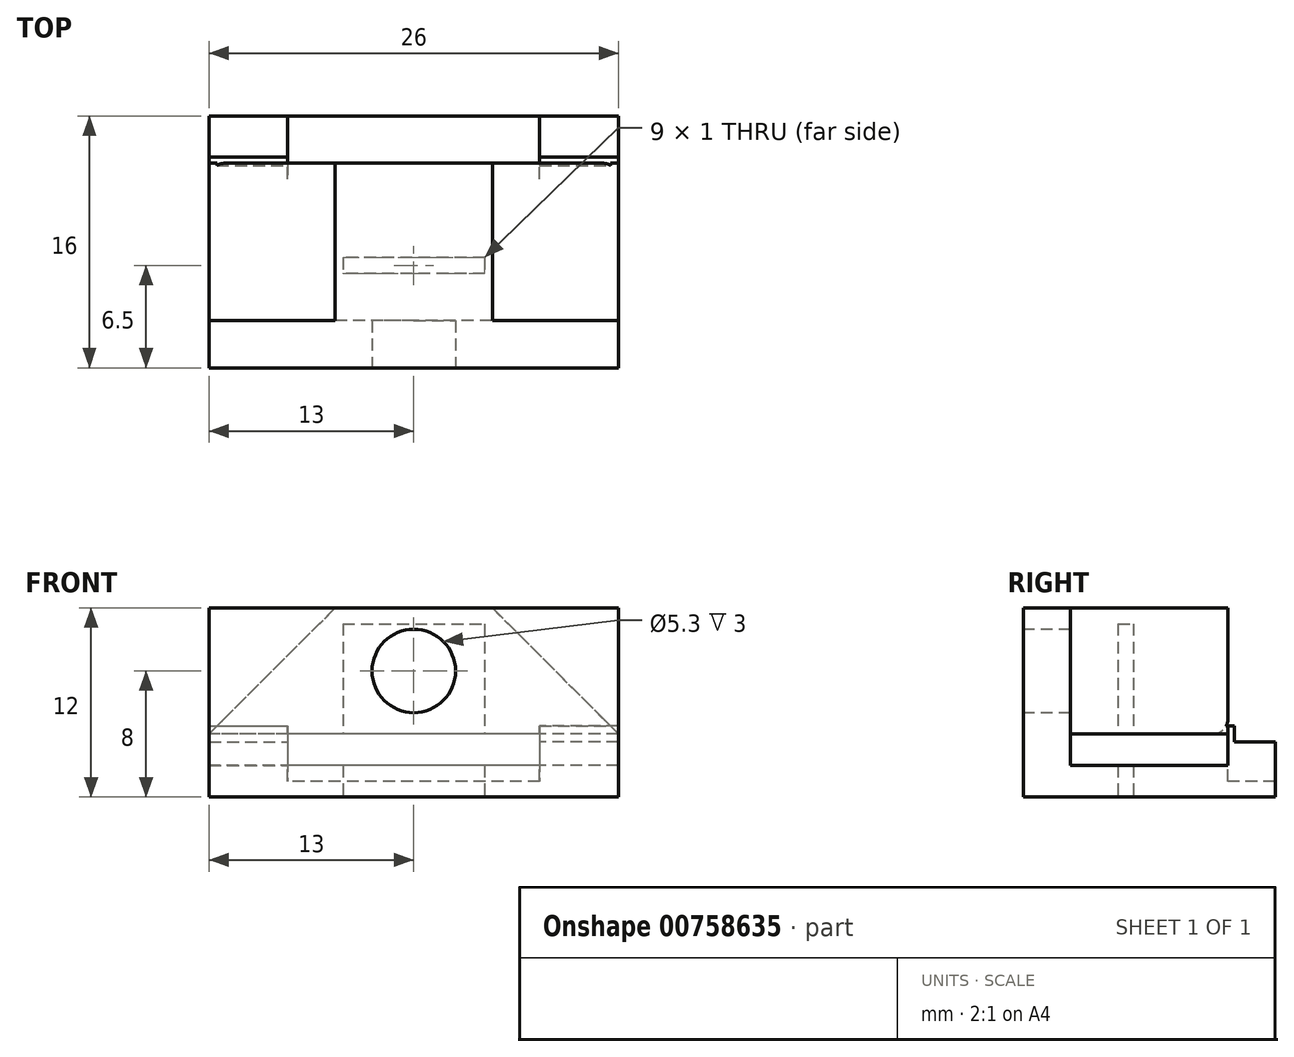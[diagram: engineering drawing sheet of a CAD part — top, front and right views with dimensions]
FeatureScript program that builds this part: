
annotation { "Feature Type Name" : "Feature", "Feature Type Description" : "" }
export const myFeature = defineFeature(function(context is Context, id is Id, definition is map)
    precondition{}
    {
        {
            var Q0;
            Q0=qCreatedBy(makeId("Front.planeOp"),FACE);
            var sketch = newSketch(context, id + "F0", { "sketchPlane" : qUnion([Q0])});
            skLineSegment(sketch, "E0.bottom", {"start": v(13, -6) * mm, "end": v(-13, -6) * mm});
            skLineSegment(sketch, "E0.top", {"start": v(13, 6) * mm, "end": v(-13, 6) * mm});
            skLineSegment(sketch, "E0.left", {"start": v(13, -6) * mm, "end": v(13, 6) * mm});
            skLineSegment(sketch, "E0.right", {"start": v(-13, -6) * mm, "end": v(-13, 6) * mm});
            skPoint(sketch, "E0.middle", {"position": v(0, 0) * mm});
            skSolve(sketch);
        }
        {
            var Q0;
            Q0 = qSketchRegion(id + "F0", true);
            extrude(context, id + "F1", {"entities" : qUnion([Q0]), "depth" : 3 * mm, "offsetDistance" : 25 * mm});
        }
        {
            var Q0;
            Q0=makeQuery(id+"F1.opExtrude","CAP_FACE",FACE,{"disambiguationData":[OSD([sQuery(id+"F0.wireOp",EDGE,"E0.bottom"),sQuery(id+"F0.wireOp",EDGE,"E0.top"),sQuery(id+"F0.wireOp",EDGE,"E0.left"),sQuery(id+"F0.wireOp",EDGE,"E0.right")])],"isStart":true});
            var sketch = newSketch(context, id + "F2", { "sketchPlane" : qUnion([Q0])});
            skLineSegment(sketch, "E1", {"start": v(0, -2) * mm, "end": v(13, -2) * mm});
            skPoint(sketch, "E1.startSnap0", {"position": v(0, 6) * mm});
            skLineSegment(sketch, "E2", {"start": v(13, -2) * mm, "end": v(5, 6) * mm});
            skLineSegment(sketch, "E3", {"start": v(5, 6) * mm, "end": v(0, 6) * mm});
            skLineSegment(sketch, "E4.MirrorCS", {"start": v(-5, 6) * mm, "end": v(0, 6) * mm});
            skLineSegment(sketch, "E5.MirrorCS", {"start": v(-13, -2) * mm, "end": v(-5, 6) * mm});
            skLineSegment(sketch, "E6.MirrorCS", {"start": v(0, -2) * mm, "end": v(-13, -2) * mm});
            skSolve(sketch);
        }
        {
            var Q0;
            Q0 = qSketchRegion(id + "F2", true);
            extrude(context, id + "F3", {"entities" : qUnion([Q0]), "depth" : 10 * mm, "offsetDistance" : 25 * mm});
        }
        {
            var Q0;
            Q0=makeQuery(id+"F1.opExtrude","CAP_FACE",FACE,{"disambiguationData":[OSD([sQuery(id+"F0.wireOp",EDGE,"E0.bottom"),sQuery(id+"F0.wireOp",EDGE,"E0.top"),sQuery(id+"F0.wireOp",EDGE,"E0.left"),sQuery(id+"F0.wireOp",EDGE,"E0.right")])],"isStart":true});
            var sketch = newSketch(context, id + "F4", { "sketchPlane" : qUnion([Q0])});
            skLineSegment(sketch, "E7.bottom", {"start": v(-13, -6) * mm, "end": v(13, -6) * mm});
            skLineSegment(sketch, "E7.top", {"start": v(-13, -4) * mm, "end": v(13, -4) * mm});
            skLineSegment(sketch, "E7.left", {"start": v(-13, -6) * mm, "end": v(-13, -4) * mm});
            skLineSegment(sketch, "E7.right", {"start": v(13, -6) * mm, "end": v(13, -4) * mm});
            skSolve(sketch);
        }
        {
            var Q0;
            Q0 = qSketchRegion(id + "F4", true);
            extrude(context, id + "F5", {"entities" : qUnion([Q0]), "operationType" : NewBodyOperationType.ADD, "depth" : 13 * mm, "offsetDistance" : 25 * mm});
        }
        {
            var Q0;
            Q0=makeQuery(id+"F5.opExtrude","SWEPT_FACE",FACE,{"disambiguationData":[OSD([sQuery(id+"F4.wireOp",EDGE,"E7.top")])]});
            var sketch = newSketch(context, id + "F6", { "sketchPlane" : qUnion([Q0])});
            skLineSegment(sketch, "E8.bottom", {"start": v(13, 13) * mm, "end": v(8, 13) * mm});
            skLineSegment(sketch, "E8.top", {"start": v(13, 10) * mm, "end": v(8, 10) * mm});
            skLineSegment(sketch, "E8.left", {"start": v(13, 13) * mm, "end": v(13, 10) * mm});
            skLineSegment(sketch, "E8.right", {"start": v(8, 13) * mm, "end": v(8, 10) * mm});
            skLineSegment(sketch, "E9.bottom", {"start": v(-13, 13) * mm, "end": v(-8, 13) * mm});
            skLineSegment(sketch, "E9.top", {"start": v(-13, 10) * mm, "end": v(-8, 10) * mm});
            skLineSegment(sketch, "E9.left", {"start": v(-13, 13) * mm, "end": v(-13, 10) * mm});
            skLineSegment(sketch, "E9.right", {"start": v(-8, 13) * mm, "end": v(-8, 10) * mm});
            skSolve(sketch);
        }
        {
            var Q0;
            Q0 = qSketchRegion(id + "F6", true);
            extrude(context, id + "F7", {"entities" : qUnion([Q0]), "operationType" : NewBodyOperationType.ADD, "depth" : 1.5 * mm, "offsetDistance" : 25 * mm});
        }
        {
            var Q0;
            Q0=makeQuery(id+"F5.opExtrude","SWEPT_FACE",FACE,{"disambiguationData":[OSD([sQuery(id+"F4.wireOp",EDGE,"E7.top")])]});
            var sketch = newSketch(context, id + "F8", { "sketchPlane" : qUnion([Q0])});
            skLineSegment(sketch, "E10.bottom", {"start": v(8, 10) * mm, "end": v(-8, 10) * mm});
            skLineSegment(sketch, "E10.top", {"start": v(8, 13) * mm, "end": v(-8, 13) * mm});
            skLineSegment(sketch, "E10.left", {"start": v(8, 10) * mm, "end": v(8, 13) * mm});
            skLineSegment(sketch, "E10.right", {"start": v(-8, 10) * mm, "end": v(-8, 13) * mm});
            skSolve(sketch);
        }
        {
            var Q0;
            Q0 = qSketchRegion(id + "F8", true);
            extrude(context, id + "F9", {"entities" : qUnion([Q0]), "operationType" : NewBodyOperationType.REMOVE, "oppositeDirection" : true, "depth" : 1 * mm, "offsetDistance" : 25 * mm});
        }
        {
            var Q0;
            Q0=makeQuery(id+"F1.opExtrude","CAP_FACE",FACE,{"disambiguationData":[OSD([sQuery(id+"F0.wireOp",EDGE,"E0.bottom"),sQuery(id+"F0.wireOp",EDGE,"E0.top"),sQuery(id+"F0.wireOp",EDGE,"E0.left"),sQuery(id+"F0.wireOp",EDGE,"E0.right")])],"isStart":false});
            var sketch = newSketch(context, id + "F10", { "sketchPlane" : qUnion([Q0])});
            skCircle(sketch, "E11", {"center": v(0, 2) * mm, "radius": 2.65 * mm});
            skSolve(sketch);
        }
        {
            var Q0;
            Q0 = qSketchRegion(id + "F10", true);
            extrude(context, id + "F11", {"entities" : qUnion([Q0]), "operationType" : NewBodyOperationType.REMOVE, "endBound" : BoundingType.UP_TO_NEXT, "oppositeDirection" : true, "depth" : 25 * mm, "offsetDistance" : 25 * mm});
        }
        {
            var Q0;
            Q0=makeQuery(id+"F5.boolean.opBoolean","MERGE",FACE,{"derivedFrom":[makeQuery(id+"F1.opExtrude","SWEPT_FACE",FACE,{"disambiguationData":[OSD([sQuery(id+"F0.wireOp",EDGE,"E0.bottom")])]}),makeQuery(id+"F5.opExtrude","SWEPT_FACE",FACE,{"disambiguationData":[OSD([sQuery(id+"F4.wireOp",EDGE,"E7.bottom")])]})]});
            var sketch = newSketch(context, id + "F12", { "sketchPlane" : qUnion([Q0])});
            skLineSegment(sketch, "E12.bottom", {"start": v(-4.5, -3) * mm, "end": v(4.5, -3) * mm});
            skLineSegment(sketch, "E12.top", {"start": v(-4.5, -4) * mm, "end": v(4.5, -4) * mm});
            skLineSegment(sketch, "E12.left", {"start": v(-4.5, -3) * mm, "end": v(-4.5, -4) * mm});
            skLineSegment(sketch, "E12.right", {"start": v(4.5, -3) * mm, "end": v(4.5, -4) * mm});
            skSolve(sketch);
        }
        {
            var Q0;
            Q0 = qSketchRegion(id + "F12", true);
            extrude(context, id + "F13", {"entities" : qUnion([Q0]), "operationType" : NewBodyOperationType.REMOVE, "oppositeDirection" : true, "depth" : 11 * mm, "offsetDistance" : 25 * mm});
        }
        {
            var Q0;
            Q0=makeQuery(id+"F7.opExtrude","CAP_FACE",FACE,{"disambiguationData":[OSD([sQuery(id+"F6.wireOp",EDGE,"E9.bottom"),sQuery(id+"F6.wireOp",EDGE,"E9.top"),sQuery(id+"F6.wireOp",EDGE,"E9.left"),sQuery(id+"F6.wireOp",EDGE,"E9.right")])],"isStart":false});
            var sketch = newSketch(context, id + "F14", { "sketchPlane" : qUnion([Q0])});
            skLineSegment(sketch, "E13.bottom", {"start": v(-13, 10) * mm, "end": v(-8, 10) * mm});
            skLineSegment(sketch, "E13.top", {"start": v(-13, 10.4) * mm, "end": v(-8, 10.4) * mm});
            skLineSegment(sketch, "E13.left", {"start": v(-13, 10) * mm, "end": v(-13, 10.4) * mm});
            skLineSegment(sketch, "E13.right", {"start": v(-8, 10) * mm, "end": v(-8, 10.4) * mm});
            skSolve(sketch);
        }
        {
            var Q0;
            Q0 = qSketchRegion(id + "F14", true);
            extrude(context, id + "F15", {"entities" : qUnion([Q0]), "operationType" : NewBodyOperationType.ADD, "depth" : 1 * mm, "offsetDistance" : 25 * mm});
        }
        {
            var Q0;
            Q0=makeQuery(id+"F7.opExtrude","CAP_FACE",FACE,{"disambiguationData":[OSD([sQuery(id+"F6.wireOp",EDGE,"E8.bottom"),sQuery(id+"F6.wireOp",EDGE,"E8.top"),sQuery(id+"F6.wireOp",EDGE,"E8.left"),sQuery(id+"F6.wireOp",EDGE,"E8.right")])],"isStart":false});
            var sketch = newSketch(context, id + "F16", { "sketchPlane" : qUnion([Q0])});
            skLineSegment(sketch, "E14.bottom", {"start": v(13, 10) * mm, "end": v(8, 10) * mm});
            skLineSegment(sketch, "E14.top", {"start": v(13, 10.4) * mm, "end": v(8, 10.4) * mm});
            skLineSegment(sketch, "E14.left", {"start": v(13, 10) * mm, "end": v(13, 10.4) * mm});
            skLineSegment(sketch, "E14.right", {"start": v(8, 10) * mm, "end": v(8, 10.4) * mm});
            skSolve(sketch);
        }
        {
            var Q0;
            Q0 = qSketchRegion(id + "F16", true);
            extrude(context, id + "F17", {"entities" : qUnion([Q0]), "operationType" : NewBodyOperationType.ADD, "depth" : 1 * mm, "offsetDistance" : 25 * mm});
        }
        {
            var Q0;
            {var subQ0=sQuery(id+"F2.wireOp",EDGE,"E6.MirrorCS");var subQ1=sQuery(id+"F2.wireOp",EDGE,"E1");var subQ2=makeQuery(id+"F3.opExtrude","CAP_FACE",FACE,{"disambiguationData":[OSD([subQ1,sQuery(id+"F2.wireOp",EDGE,"E2"),sQuery(id+"F2.wireOp",EDGE,"E3"),sQuery(id+"F2.wireOp",EDGE,"E4.MirrorCS"),sQuery(id+"F2.wireOp",EDGE,"E5.MirrorCS"),subQ0])],"isStart":false});Q0=makeQuery(id+"F17.boolean.opBoolean","SPLIT",EDGE,{"disambiguationData":[topologyDisambiguationEdgeConnected([subQ2])],"derivedFrom":makeQuery(id+"F15.boolean.opBoolean","SPLIT",EDGE,{"disambiguationData":[topologyDisambiguationEdgeConnected([subQ2])],"derivedFrom":makeQuery(id+"F3.opExtrude","CAP_EDGE",EDGE,{"disambiguationData":[OSD([subQ1,subQ0])],"isStart":false})})});}
            fillet(context, id + "F18", {"entities" : qUnion([Q0]), "radius" : 1 * mm, "tangentPropagation" : true, "allowEdgeOverflow" : false});
        }
    });
